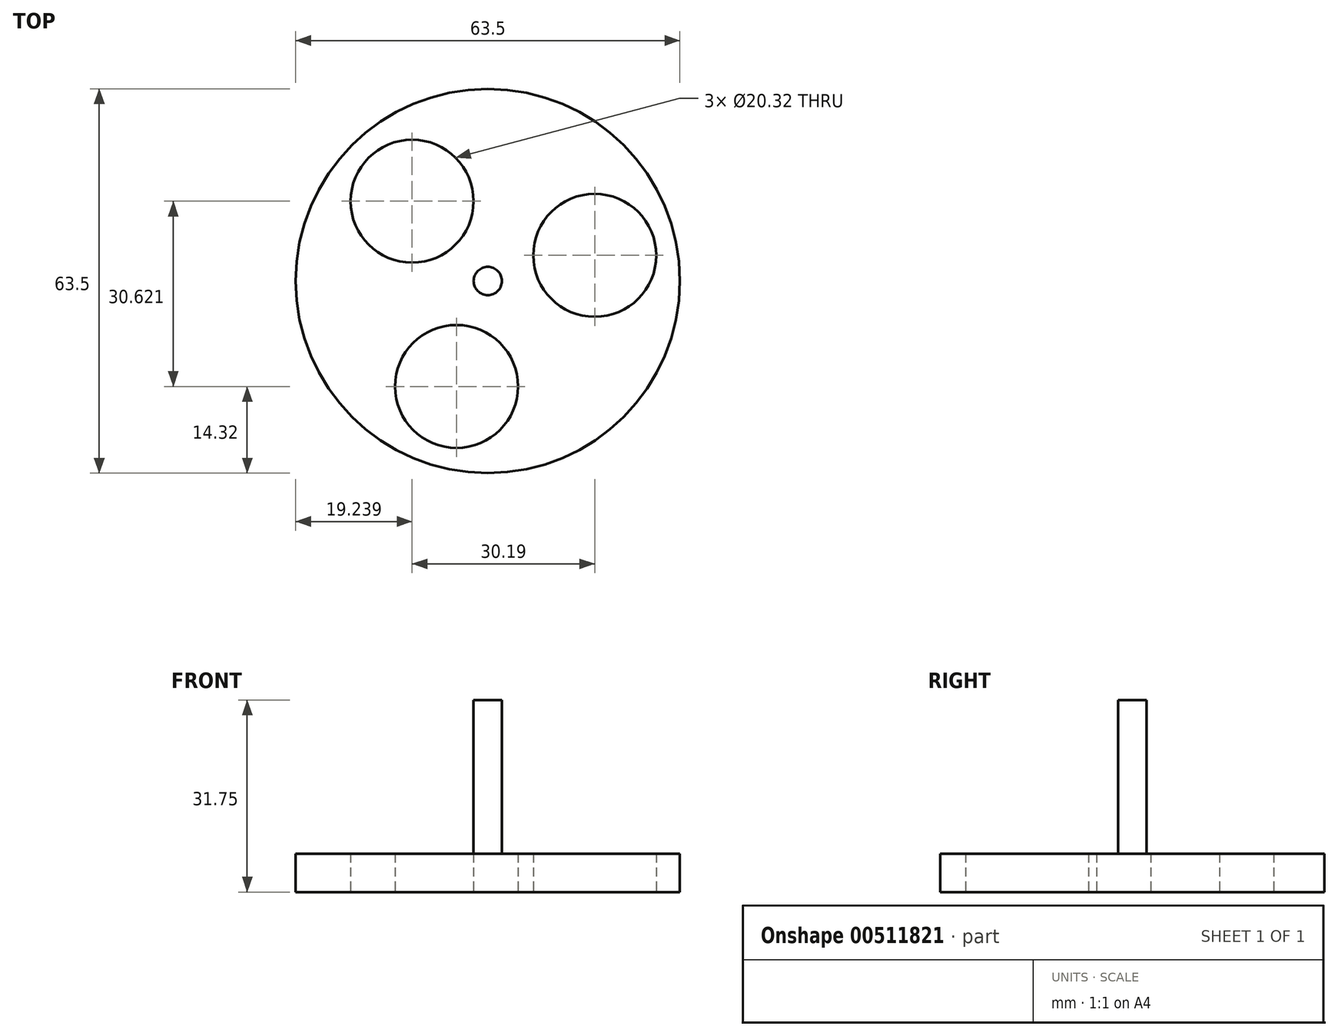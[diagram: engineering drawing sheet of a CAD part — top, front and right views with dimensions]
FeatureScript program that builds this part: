
annotation { "Feature Type Name" : "Feature", "Feature Type Description" : "" }
export const myFeature = defineFeature(function(context is Context, id is Id, definition is map)
    precondition{}
    {
        {
            var Q0;
            Q0=qCreatedBy(makeId("Top.planeOp"),FACE);
            var sketch = newSketch(context, id + "F0", { "sketchPlane" : qUnion([Q0])});
            skCircle(sketch, "E0", {"center": v(0, 0) * mm, "radius": 31.75 * mm});
            skSolve(sketch);
        }
        {
            var Q0;
            Q0=makeQuery(id+"F0.imprint","IMPRINT",FACE,{"disambiguationData":[TD([[makeQuery(id+"F0.imprint","IMPRINT",EDGE,{"derivedFrom":sQuery(id+"F0.wireOp",EDGE,"E0")}),1.0]])]});
            var sketch = newSketch(context, id + "F1", { "sketchPlane" : qUnion([Q0])});
            skCircle(sketch, "E1", {"center": v(-12.51, 13.2) * mm, "radius": 10.16 * mm});
            skCircle(sketch, "E2.1.0", {"center": v(-5.17, -17.43) * mm, "radius": 10.16 * mm});
            skCircle(sketch, "E2.2.0", {"center": v(17.68, 4.24) * mm, "radius": 10.16 * mm});
            skPoint(sketch, "E2.center", {"position": v(0, 0) * mm});
            skSolve(sketch);
        }
        {
            var Q0;
            Q0=makeQuery(id+"F0.imprint","IMPRINT",FACE,{"disambiguationData":[TD([[makeQuery(id+"F0.imprint","IMPRINT",EDGE,{"derivedFrom":sQuery(id+"F0.wireOp",EDGE,"E0")}),1.0]])]});
            extrude(context, id + "F2", {"entities" : qUnion([Q0]), "depth" : 6.35 * mm});
        }
        {
            var Q0;
            Q0=makeQuery(id+"F1.imprint","IMPRINT",FACE,{"disambiguationData":[TD([[makeQuery(id+"F1.imprint","IMPRINT",EDGE,{"derivedFrom":sQuery(id+"F1.wireOp",EDGE,"E2.1.0")}),1.0]])]});
            var Q1;
            Q1=makeQuery(id+"F1.imprint","IMPRINT",FACE,{"disambiguationData":[TD([[makeQuery(id+"F1.imprint","IMPRINT",EDGE,{"derivedFrom":sQuery(id+"F1.wireOp",EDGE,"E2.2.0")}),1.0]])]});
            var Q2;
            Q2=makeQuery(id+"F1.imprint","IMPRINT",FACE,{"disambiguationData":[TD([[makeQuery(id+"F1.imprint","IMPRINT",EDGE,{"derivedFrom":sQuery(id+"F1.wireOp",EDGE,"E1")}),1.0]])]});
            extrude(context, id + "F3", {"entities" : qUnion([Q0, Q1, Q2]), "operationType" : NewBodyOperationType.REMOVE, "depth" : 25.4 * mm});
        }
        {
            var Q0;
            Q0=makeQuery(id+"F2.opExtrude","CAP_FACE",FACE,{"disambiguationData":[OSD([sQuery(id+"F0.wireOp",EDGE,"E0")])],"isStart":false});
            var sketch = newSketch(context, id + "F4", { "sketchPlane" : qUnion([Q0])});
            skCircle(sketch, "E3", {"center": v(0, 0) * mm, "radius": 2.34 * mm});
            skSolve(sketch);
        }
        {
            var Q0;
            Q0=makeQuery(id+"F4.imprint","IMPRINT",FACE,{"disambiguationData":[TD([[makeQuery(id+"F4.imprint","IMPRINT",EDGE,{"derivedFrom":sQuery(id+"F4.wireOp",EDGE,"E3")}),1.0]])]});
            extrude(context, id + "F5", {"entities" : qUnion([Q0]), "operationType" : NewBodyOperationType.ADD, "depth" : 25.4 * mm});
        }
    });
